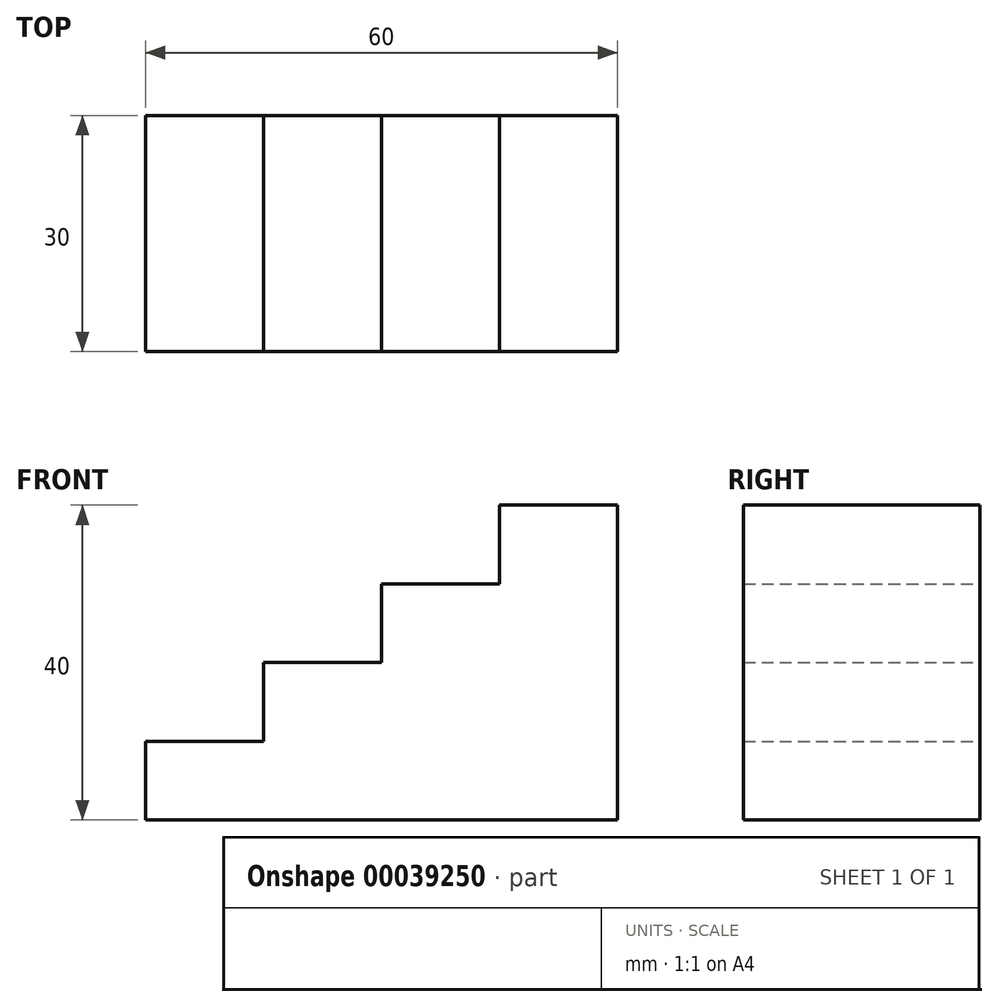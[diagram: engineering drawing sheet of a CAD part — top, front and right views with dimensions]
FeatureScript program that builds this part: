
annotation { "Feature Type Name" : "Feature", "Feature Type Description" : "" }
export const myFeature = defineFeature(function(context is Context, id is Id, definition is map)
    precondition{}
    {
        {
            var Q0;
            Q0=qCreatedBy(makeId("Front.planeOp"),FACE);
            var sketch = newSketch(context, id + "F0", { "sketchPlane" : qUnion([Q0])});
            skLineSegment(sketch, "E0.bottom", {"start": v(-28.3, -20) * mm, "end": v(31.7, -20) * mm});
            skLineSegment(sketch, "E0.top", {"start": v(16.7, 20) * mm, "end": v(31.7, 20) * mm});
            skLineSegment(sketch, "E0.left", {"start": v(-28.3, -20) * mm, "end": v(-28.3, -10) * mm});
            skLineSegment(sketch, "E0.right", {"start": v(31.7, -20) * mm, "end": v(31.7, 20) * mm});
            skLineSegment(sketch, "E1", {"start": v(-28.3, -10) * mm, "end": v(-13.3, -10) * mm});
            skLineSegment(sketch, "E2", {"start": v(-13.3, -10) * mm, "end": v(-13.3, 0) * mm});
            skLineSegment(sketch, "E3", {"start": v(-13.3, 0) * mm, "end": v(1.7, 0) * mm});
            skLineSegment(sketch, "E4", {"start": v(1.7, 0) * mm, "end": v(1.7, 10) * mm});
            skLineSegment(sketch, "E5", {"start": v(1.7, 10) * mm, "end": v(16.7, 10) * mm});
            skLineSegment(sketch, "E6", {"start": v(16.7, 10) * mm, "end": v(16.7, 20) * mm});
            skSolve(sketch);
        }
        {
            var Q0;
            Q0=makeQuery(id+"F0.imprint","IMPRINT",FACE,{"disambiguationData":[TD([[makeQuery(id+"F0.imprint","IMPRINT",EDGE,{"derivedFrom":sQuery(id+"F0.wireOp",EDGE,"E0.bottom")}),1.0]])]});
            extrude(context, id + "F1", {"entities" : qUnion([Q0]), "depth" : 30 * mm});
        }
    });
